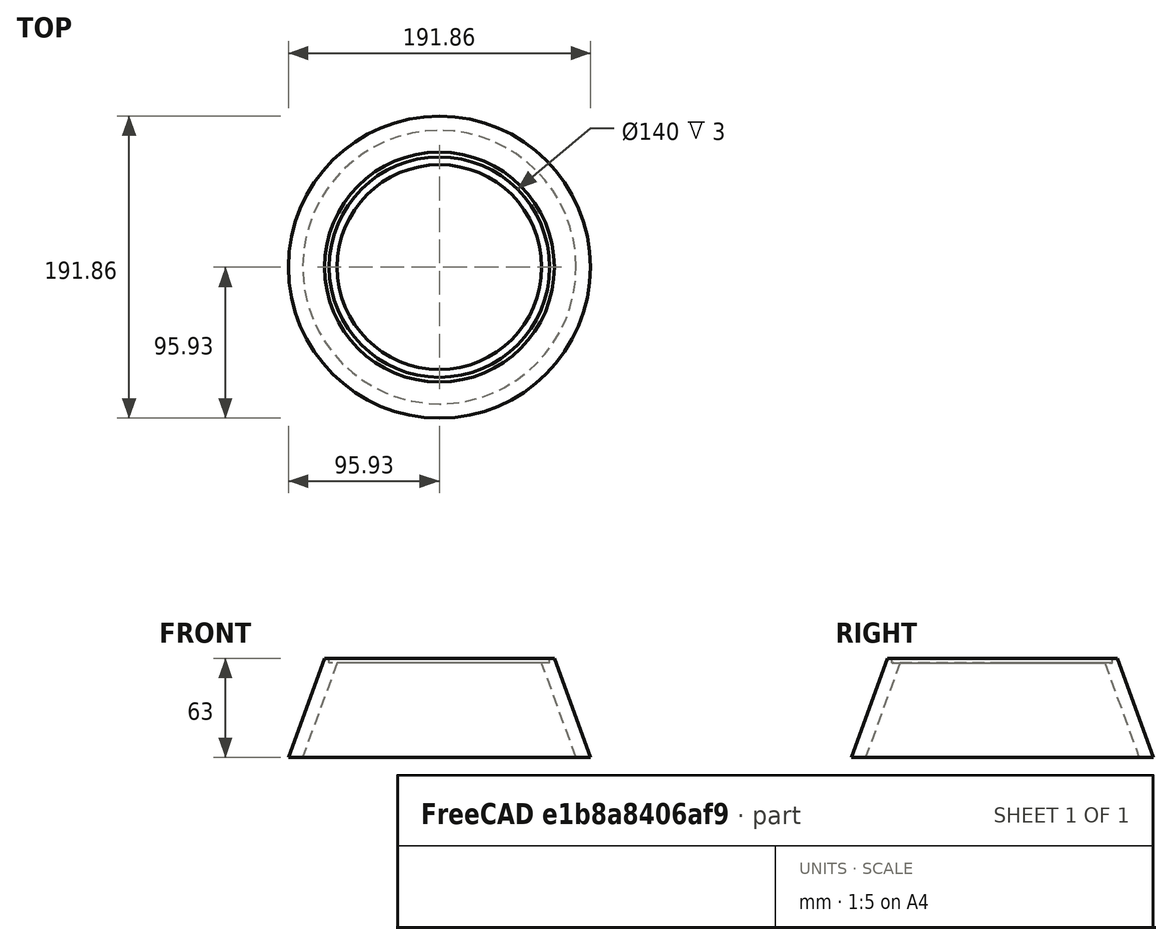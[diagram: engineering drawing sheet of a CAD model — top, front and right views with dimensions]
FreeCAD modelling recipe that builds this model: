
FCSTD DOCUMENT  (FreeCAD 0.16R6706 (Git))
Label: base_cover
License: All rights reserved
LicenseURL: http://en.wikipedia.org/wiki/All_rights_reserved
objects: Sketcher::SketchObject×1, PartDesign::Revolution×1
note: 3 computed .brp shape members not serialized (recipe doc carries the construction recipe); baked Part::Feature solids carry a one-line shape summary decoded from their .brp

FEATURE [Sketcher::SketchObject] Sketch
  Placement = pos=(0,0,0) rot=(-1,0,0;4.71239rad)
  sketch-geometry (7):
    g0: LineSegment [constr] StartX=0 StartY=0 StartZ=0 EndX=65 EndY=0 EndZ=0
    g1: LineSegment StartX=65 StartY=0 StartZ=0 EndX=70 EndY=0 EndZ=0
    g2: LineSegment StartX=70 StartY=0 StartZ=0 EndX=70 EndY=3 EndZ=0
    g3: LineSegment StartX=70 StartY=3 StartZ=0 EndX=73 EndY=3 EndZ=0
    g4: LineSegment StartX=73 StartY=3 StartZ=0 EndX=95.9301 EndY=-60 EndZ=0
    g5: LineSegment StartX=95.9301 StartY=-60 StartZ=0 EndX=86.8382 EndY=-60 EndZ=0
    g6: LineSegment StartX=86.8382 StartY=-60 StartZ=0 EndX=65 EndY=0 EndZ=0
  constraints (20):
    c: Coincident(g0,g-1)
    c: Horizontal(g0)
    c: Distance(g0) = 65
    c: Coincident(g0,g1)
    c: Horizontal(g1)
    c: Coincident(g1,g2)
    c: Vertical(g2)
    c: Coincident(g2,g3)
    c: Horizontal(g3)
    c: Coincident(g3,g4)
    c: Coincident(g4,g5)
    c: Horizontal(g5)
    c: Coincident(g5,g6)
    c: Coincident(g6,g1)
    c: Parallel(g6,g4)
    c: Distance(g2) = 3
    c: Distance(g3) = 3
    c: Distance(g1) = 5
    c: DistanceY(g5,g1) = 60
    c: Angle(g6) = 1.91986
FEATURE [PartDesign::Revolution] Revolution
  Angle = 360
  Axis = (0,0,1)
  Base = (0,0,0)
  Placement = pos=(0,0,0) rot=(-1,0,0;4.71239rad)
  ReferenceAxis = -> Sketch [V_Axis]
  Reversed = true
  Sketch = -> Sketch
